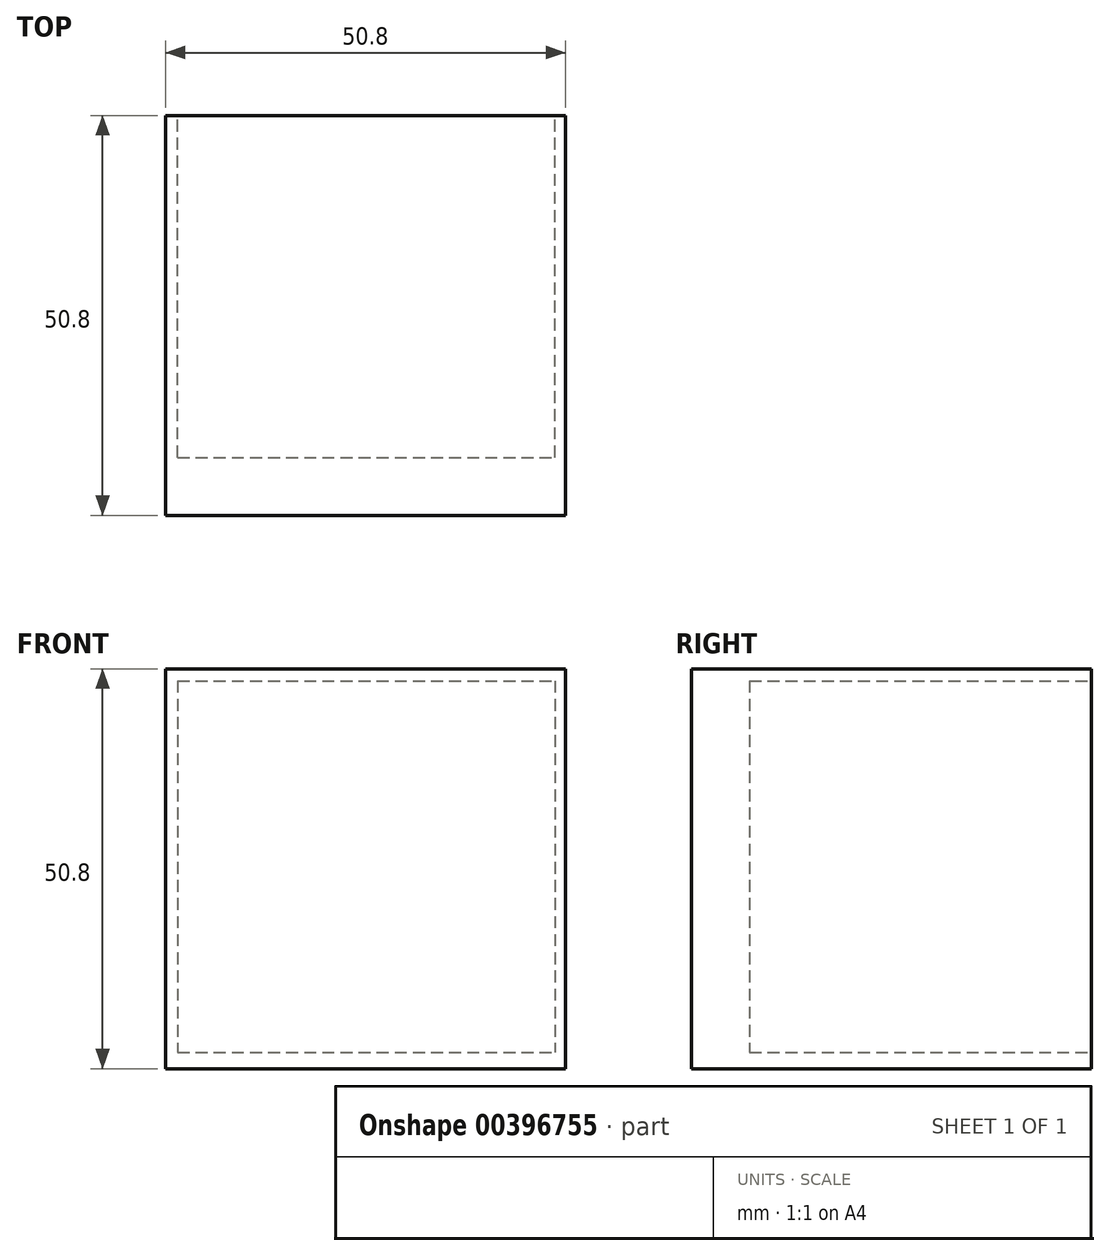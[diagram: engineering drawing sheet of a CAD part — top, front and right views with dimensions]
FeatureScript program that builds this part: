
annotation { "Feature Type Name" : "Feature", "Feature Type Description" : "" }
export const myFeature = defineFeature(function(context is Context, id is Id, definition is map)
    precondition{}
    {
        {
            var Q0;
            Q0=qCreatedBy(makeId("Right.planeOp"),FACE);
            var sketch = newSketch(context, id + "F0", { "sketchPlane" : qUnion([Q0])});
            skLineSegment(sketch, "E0.bottom", {"start": v(0, 0) * mm, "end": v(-50.8, 0) * mm});
            skLineSegment(sketch, "E0.top", {"start": v(0, 50.8) * mm, "end": v(-50.8, 50.8) * mm});
            skLineSegment(sketch, "E0.left", {"start": v(0, 0) * mm, "end": v(0, 50.8) * mm});
            skLineSegment(sketch, "E0.right", {"start": v(-50.8, 0) * mm, "end": v(-50.8, 50.8) * mm});
            skSolve(sketch);
        }
        {
            var Q0;
            Q0 = qSketchRegion(id + "F0", true);
            extrude(context, id + "F1", {"entities" : qUnion([Q0]), "depth" : 50.8 * mm});
        }
        {
            var Q0;
            Q0=qCreatedBy(makeId("Front.planeOp"),FACE);
            var sketch = newSketch(context, id + "F2", { "sketchPlane" : qUnion([Q0])});
            skLineSegment(sketch, "E1.bottom", {"start": v(1.53, 49.27) * mm, "end": v(49.46, 49.27) * mm});
            skLineSegment(sketch, "E1.top", {"start": v(1.53, 2.1) * mm, "end": v(49.46, 2.1) * mm});
            skLineSegment(sketch, "E1.left", {"start": v(1.53, 49.27) * mm, "end": v(1.53, 2.1) * mm});
            skLineSegment(sketch, "E1.right", {"start": v(49.46, 49.27) * mm, "end": v(49.46, 2.1) * mm});
            skSolve(sketch);
        }
        {
            var Q0;
            Q0 = qSketchRegion(id + "F2", true);
            extrude(context, id + "F3", {"entities" : qUnion([Q0]), "operationType" : NewBodyOperationType.REMOVE, "depth" : 43.43 * mm});
        }
    });
